# Revit family: ledfloodmo-p_re570-300w-857-as_709000060200
name_source: partatom
category: Leuchten
revit_build: Autodesk Revit 2016 (Build: 20190508_0715(x64)
units: mm (PartAtom-declared; Revit-internal decimal feet)

## family parameters
Basisbauteil = Fläche
Beim Laden mit Abzugskörper schneiden = Nein
Bemaßung runder Anschluss = Durchmesser verwenden
Gemeinsam genutzt = Nein
Lichtquelle = Nein
Raumberechnungspunkt = Nein
Teiletyp = Normal

## types (1)
- LEDFloodMo-P Re570-300W-857-AS (1 x LED, 42000 lm)
    Approval mark = CE
    Beschreibung = Precise modular optical design for area, object and facade lighting. Super slim aluminium body with integrated heatsink. Robust design with high protection against water and dust. High energy saving up to 65% compared to halogen and high pressure sodium lamps. IP66 and suitable for use on the coastal applications.
    CIE Flux Codes = 60 86 97 99 100
    Control Gear = Electronic ballast
    Height = 54 mm
    Hersteller = OPPLE
    Lamp Light Flux = 42000 lm
    Lamp count = 1
    Lampe = 1 x LED
    Length = 521 mm
    Luminous efficacy = 140 lm/W
    ModVariant = Nein
    Modell = 709000060200
    Mounting Place = Pole
    Mounting Type = Pole top
    Number of Poles = 1
    OnlyDefault = Ja
    Power Factor = 1
    Product Name = LEDFloodMo-P Re570-300W-857-AS
    Product group = Floodlight Modulo Performer
    ProductGroupID = 2006
    Protection Class = Protection class I
    Protection Degree = IP 66
    RLX_Detail_Level = 1
    RlxData = <blob elided: 190057 chars, md5=80c4c8f4>
    Scheinlast = 300 VA
    Socket = socket
    Standby Power = 0 W
    System Light Flux = 42000 lm
    System Power = 300 W
    Typenbild = modulo_re570.jpg
    Typenkommentare = Product without accessories
    URL = http://relux.com
    VarID = ---
    Voltage = 230 V
    Voltage Range = 220-240 V
    Vorgabe-Ansicht = 1800 mm
    Weight = 0.00 kg
    Width = 400 mm

## geometry (parser evidence)
native form markers: Blend x4, Sweep x11
no freeform markers — native parametric forms only
